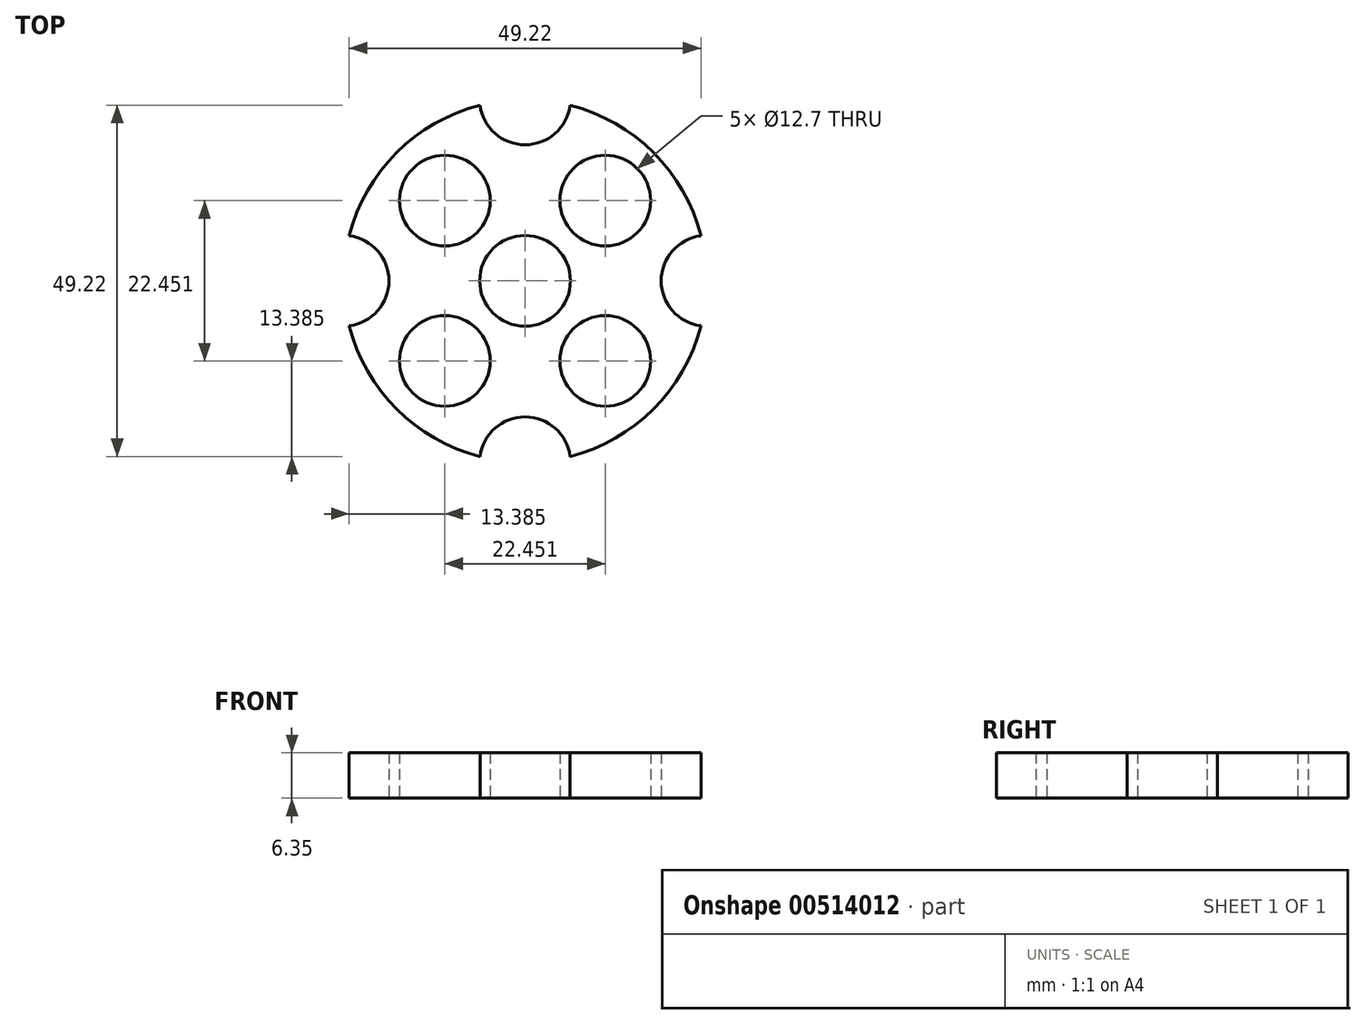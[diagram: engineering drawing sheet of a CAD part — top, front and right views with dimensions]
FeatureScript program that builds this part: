
annotation { "Feature Type Name" : "Feature", "Feature Type Description" : "" }
export const myFeature = defineFeature(function(context is Context, id is Id, definition is map)
    precondition{}
    {
        {
            var Q0;
            Q0=qCreatedBy(makeId("Top.planeOp"),FACE);
            var sketch = newSketch(context, id + "F0", { "sketchPlane" : qUnion([Q0])});
            skArc(sketch, "E0", {"start": v(-6.3, 24.6) * mm, "mid": v(-17.96, 17.96) * mm, "end": v(-24.6, 6.3) * mm});
            skArc(sketch, "E1", {"start": v(-6.3, 24.6) * mm, "mid": v(0, 19.05) * mm, "end": v(6.3, 24.6) * mm});
            skArc(sketch, "E2", {"start": v(24.6, 6.3) * mm, "mid": v(19.05, 0) * mm, "end": v(24.6, -6.3) * mm});
            skArc(sketch, "E3", {"start": v(6.3, -24.6) * mm, "mid": v(0, -19.05) * mm, "end": v(-6.3, -24.6) * mm});
            skArc(sketch, "E4", {"start": v(-24.6, -6.3) * mm, "mid": v(-19.05, 0) * mm, "end": v(-24.6, 6.3) * mm});
            skArc(sketch, "E5.trimOffspring", {"start": v(-24.6, -6.3) * mm, "mid": v(-17.96, -17.96) * mm, "end": v(-6.3, -24.6) * mm});
            skArc(sketch, "E6.trimOffspring", {"start": v(24.6, 6.3) * mm, "mid": v(17.96, 17.96) * mm, "end": v(6.3, 24.6) * mm});
            skArc(sketch, "E7.trimOffspring", {"start": v(6.3, -24.6) * mm, "mid": v(17.96, -17.96) * mm, "end": v(24.6, -6.3) * mm});
            skCircle(sketch, "E8", {"center": v(0, 0) * mm, "radius": 6.35 * mm});
            skCircle(sketch, "E9", {"center": v(-11.23, 11.23) * mm, "radius": 6.35 * mm});
            skCircle(sketch, "E10", {"center": v(11.23, 11.23) * mm, "radius": 6.35 * mm});
            skCircle(sketch, "E11", {"center": v(11.23, -11.23) * mm, "radius": 6.35 * mm});
            skCircle(sketch, "E12", {"center": v(-11.23, -11.23) * mm, "radius": 6.35 * mm});
            skPoint(sketch, "E13.start.orphan", {"position": v(-17.96, 17.96) * mm});
            skPoint(sketch, "E14.orphan", {"position": v(-4.5, 4.5) * mm});
            skPoint(sketch, "E15.trimOffspring.end.orphan", {"position": v(-4.5, -4.5) * mm});
            skPoint(sketch, "E16.trimOffspring.end.orphan", {"position": v(17.96, 17.96) * mm});
            skPoint(sketch, "E17.orphan", {"position": v(17.96, -17.96) * mm});
            skPoint(sketch, "E18.trimOffspring.start.orphan", {"position": v(4.5, -4.5) * mm});
            skPoint(sketch, "E19.trimOffspring.start.orphan", {"position": v(4.5, 4.5) * mm});
            skPoint(sketch, "E20.start.orphan", {"position": v(-17.96, -17.96) * mm});
            skSolve(sketch);
        }
        {
            var Q0;
            Q0=makeQuery(id+"F0.imprint","IMPRINT",FACE,{"disambiguationData":[TD([[makeQuery(id+"F0.imprint","IMPRINT",EDGE,{"derivedFrom":sQuery(id+"F0.wireOp",EDGE,"E0")}),1.0]])]});
            extrude(context, id + "F1", {"entities" : qUnion([Q0]), "depth" : 6.35 * mm});
        }
    });
